# Revit family: Kessel 917413 en
name_source: partatom
category: Sanitärinstallationen
revit_build: Autodesk Revit 2017 (Build: 20160225_1515(x64)
units: mm (PartAtom-declared; Revit-internal decimal feet)

## family parameters
Arbeitsebenenbasiert = Nein
Beim Laden mit Abzugskörper schneiden = Nein
Bemaßung runder Anschluss = Durchmesser verwenden
Gemeinsam genutzt = Nein
Immer vertikal = Ja
Raumberechnungspunkt = Nein
Teiletyp = Normal

## types (1)
- Kessel 917413 en
    <1.010.00.2> Number of the part of the guideline = 98
    <1.010.00.3> Issue date (month) of the guideline = 200601
    <1.010.00.4> Manufacturer name = Kessel
    <1.010.00.5> Revision date of the file = 20190227
    <1.800.00.3> BS number = 10000100000000000000000000000000000000000000000004000
    <1.800.00.4> Comment field = Einbauschrank zur Aufputzmontage
    <1.810.00.3> Manufacturer’s reference number = 917413
    <1.810.00.4> DATANORM number = 917413
    <1.810.00.6> GTIN number = 4026092035597
    <1.960/3L.00.8> Link (URL) = http://www.kessel.de
    <98.100.00.4> Area of application = Zubehör
    <98.110.00.4> Product series = Zubehör
    <98.700.00.4> Product name = Einbauschrank zur Aufputzmontage
    CONNECTOR0_DIAMETER_dY_0r = 0 mm  [stored 0 ft]
    CONNECTOR0_dY_01 = 1 mm  [stored 0.00328084 ft]
    CONNECTOR0_ref_dX = 175 mm  [stored 0.574147 ft]
    CONNECTOR0_ref_dY = 1 mm  [stored 0.00328084 ft]
    CONNECTOR0_ref_dZ = 100 mm  [stored 0.328084 ft]
    CONNECTOR1_DIAMETER_dY_0r = 0 mm  [stored 0 ft]
    CONNECTOR1_dY_01 = 1 mm  [stored 0.00328084 ft]
    CONNECTOR1_ref_dX = 175 mm  [stored 0.574147 ft]
    CONNECTOR1_ref_dY = 1 mm  [stored 0.00328084 ft]
    CONNECTOR1_ref_dZ = 100 mm  [stored 0.328084 ft]
    Hersteller = Kessel
    Modell = 917413
    URL = www.kessel.de

note: [stored X ft] marks values corroborated as IEEE doubles in the binary element streams (Revit-internal decimal feet)

## geometry (parser evidence)
native form markers: Sweep x2
no freeform markers — native parametric forms only
